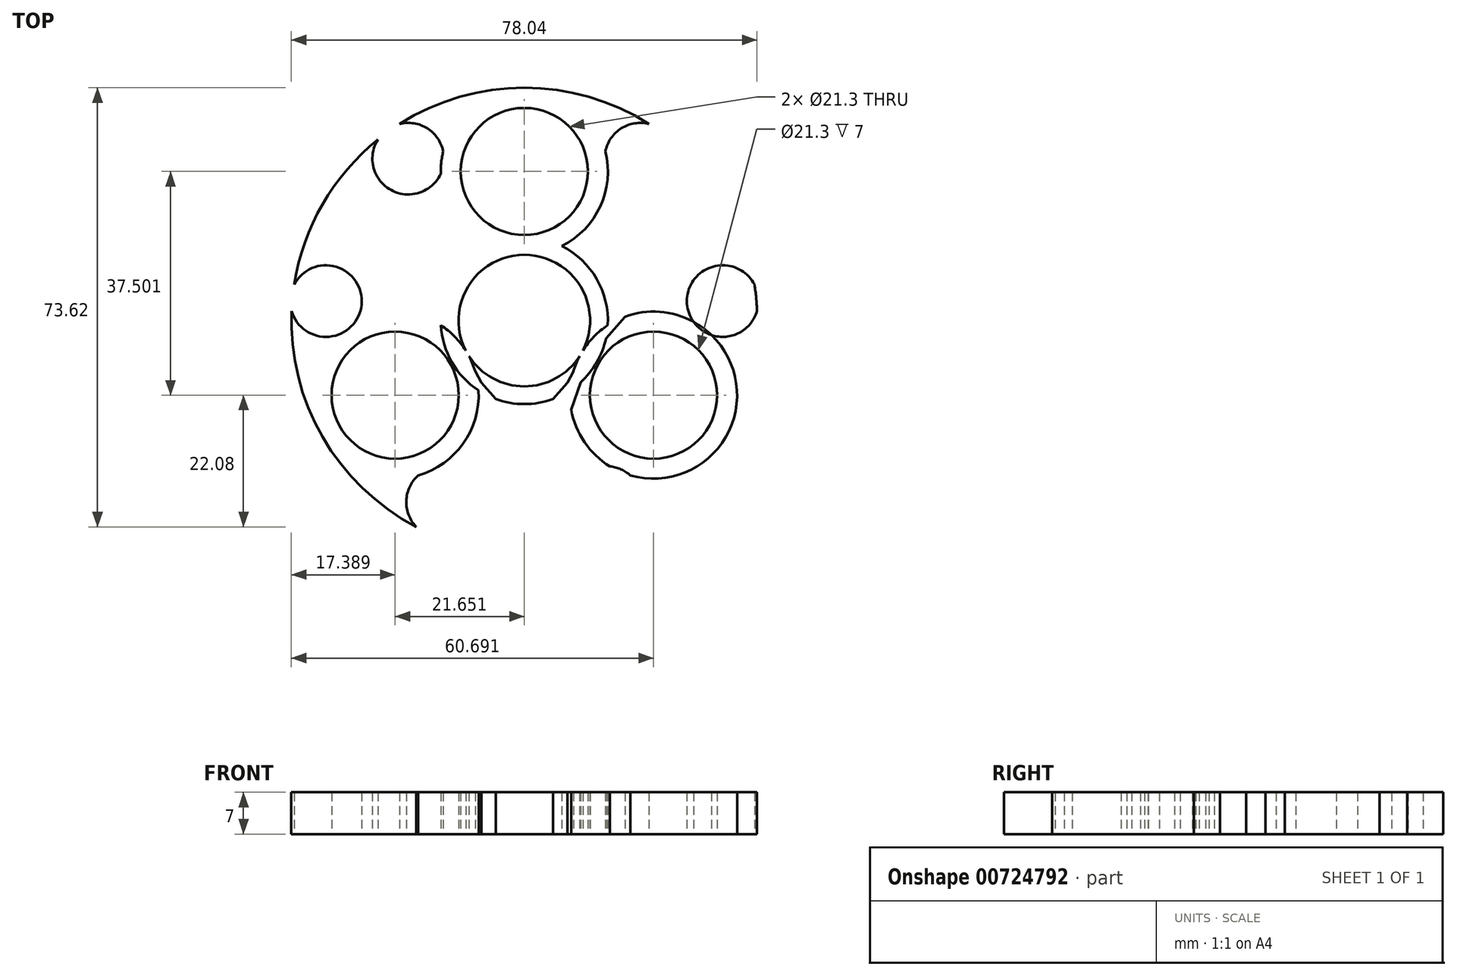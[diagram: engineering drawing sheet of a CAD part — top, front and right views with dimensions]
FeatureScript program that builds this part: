
annotation { "Feature Type Name" : "Feature", "Feature Type Description" : "" }
export const myFeature = defineFeature(function(context is Context, id is Id, definition is map)
    precondition{}
    {
        {
            var Q0;
            Q0=qCreatedBy(makeId("Top.planeOp"),FACE);
            var sketch = newSketch(context, id + "F0", { "sketchPlane" : qUnion([Q0])});
            skCircle(sketch, "E0", {"center": v(0, 0) * mm, "radius": 11.03 * mm});
            skCircle(sketch, "E1", {"center": v(0, 0) * mm, "radius": 14 * mm});
            skCircle(sketch, "E2", {"center": v(0, 25) * mm, "radius": 10.65 * mm});
            skCircle(sketch, "E3", {"center": v(0, 25) * mm, "radius": 14 * mm});
            skCircle(sketch, "E4.1.2", {"center": v(-21.65, -12.5) * mm, "radius": 14 * mm});
            skCircle(sketch, "E4.1.3", {"center": v(-21.65, -12.5) * mm, "radius": 10.65 * mm});
            skCircle(sketch, "E4.2.2", {"center": v(21.65, -12.5) * mm, "radius": 14 * mm});
            skCircle(sketch, "E4.2.3", {"center": v(21.65, -12.5) * mm, "radius": 10.65 * mm});
            skCircle(sketch, "E5", {"center": v(0, 0) * mm, "radius": 39.04 * mm});
            skCircle(sketch, "E6", {"center": v(-19.46, 27.15) * mm, "radius": 6 * mm});
            skCircle(sketch, "E7.MirrorC", {"center": v(19.46, 27.15) * mm, "radius": 6 * mm});
            skCircle(sketch, "E8.1.0", {"center": v(-13.78, -30.42) * mm, "radius": 6 * mm});
            skCircle(sketch, "E8.1.1", {"center": v(-33.24, 3.28) * mm, "radius": 6 * mm});
            skCircle(sketch, "E8.2.0", {"center": v(33.24, 3.28) * mm, "radius": 6 * mm});
            skCircle(sketch, "E8.2.1", {"center": v(13.78, -30.42) * mm, "radius": 6 * mm});
            skSolve(sketch);
        }
        {
            var Q0;
            {var subQ0=sQuery(id+"F0.wireOp",EDGE,"E6");var subQ1=sQuery(id+"F0.wireOp",EDGE,"E3");var subQ2=makeQuery(id+"F0.imprint","INTERSECT",VERTEX,{"disambiguationData":[OD(0.0)],"derivedFrom":[subQ1,subQ0]});Q0=makeQuery(id+"F0.imprint","IMPRINT",FACE,{"disambiguationData":[TD([[makeQuery(id+"F0.imprint","IMPRINT",EDGE,{"disambiguationData":[TD([[subQ2,1.0]])],"derivedFrom":subQ1}),-1.0]])]});}
            var Q1;
            {var subQ0=sQuery(id+"F0.wireOp",EDGE,"E8.1.0");var subQ1=sQuery(id+"F0.wireOp",EDGE,"E4.1.2");var subQ2=makeQuery(id+"F0.imprint","INTERSECT",VERTEX,{"disambiguationData":[OD(0.0)],"derivedFrom":[subQ1,subQ0]});Q1=makeQuery(id+"F0.imprint","IMPRINT",FACE,{"disambiguationData":[TD([[makeQuery(id+"F0.imprint","IMPRINT",EDGE,{"disambiguationData":[TD([[subQ2,1.0]])],"derivedFrom":subQ1}),-1.0]])]});}
            var Q2;
            {var subQ0=sQuery(id+"F0.wireOp",EDGE,"E8.2.0");var subQ1=sQuery(id+"F0.wireOp",EDGE,"E4.2.2");var subQ2=makeQuery(id+"F0.imprint","INTERSECT",VERTEX,{"disambiguationData":[OD(0.0)],"derivedFrom":[subQ1,subQ0]});Q2=makeQuery(id+"F0.imprint","IMPRINT",FACE,{"disambiguationData":[TD([[makeQuery(id+"F0.imprint","IMPRINT",EDGE,{"disambiguationData":[TD([[subQ2,1.0]])],"derivedFrom":subQ1}),-1.0]])]});}
            var Q3;
            Q3=makeQuery(id+"F0.imprint","IMPRINT",FACE,{"disambiguationData":[TD([[makeQuery(id+"F0.imprint","IMPRINT",EDGE,{"derivedFrom":sQuery(id+"F0.wireOp",EDGE,"E2")}),-1.0]])]});
            var Q4;
            {var subQ0=sQuery(id+"F0.wireOp",EDGE,"E0");var subQ1=sQuery(id+"F0.wireOp",EDGE,"E3");var subQ2=makeQuery(id+"F0.imprint","INTERSECT",VERTEX,{"disambiguationData":[OD(1.0)],"derivedFrom":[subQ1,subQ0]});Q4=makeQuery(id+"F0.imprint","IMPRINT",FACE,{"disambiguationData":[TD([[makeQuery(id+"F0.imprint","IMPRINT",EDGE,{"disambiguationData":[TD([[subQ2,-1.0]])],"derivedFrom":subQ1}),-1.0]])]});}
            var Q5;
            {var subQ0=sQuery(id+"F0.wireOp",EDGE,"E1");var subQ1=sQuery(id+"F0.wireOp",EDGE,"E3");var subQ2=makeQuery(id+"F0.imprint","INTERSECT",VERTEX,{"disambiguationData":[OD(0.0)],"derivedFrom":[subQ1,subQ0]});Q5=makeQuery(id+"F0.imprint","IMPRINT",FACE,{"disambiguationData":[TD([[makeQuery(id+"F0.imprint","IMPRINT",EDGE,{"disambiguationData":[TD([[subQ2,-1.0]])],"derivedFrom":subQ1}),-1.0]])]});}
            var Q6;
            {var subQ0=sQuery(id+"F0.wireOp",EDGE,"E1");var subQ1=sQuery(id+"F0.wireOp",EDGE,"E4.1.2");var subQ2=makeQuery(id+"F0.imprint","INTERSECT",VERTEX,{"disambiguationData":[OD(0.0)],"derivedFrom":[subQ1,subQ0]});Q6=makeQuery(id+"F0.imprint","IMPRINT",FACE,{"disambiguationData":[TD([[makeQuery(id+"F0.imprint","IMPRINT",EDGE,{"disambiguationData":[TD([[subQ2,-1.0]])],"derivedFrom":subQ1}),1.0]])]});}
            var Q7;
            {var subQ0=sQuery(id+"F0.wireOp",EDGE,"E1");var subQ1=sQuery(id+"F0.wireOp",EDGE,"E4.1.2");var subQ2=makeQuery(id+"F0.imprint","INTERSECT",VERTEX,{"disambiguationData":[OD(0.0)],"derivedFrom":[subQ1,subQ0]});Q7=makeQuery(id+"F0.imprint","IMPRINT",FACE,{"disambiguationData":[TD([[makeQuery(id+"F0.imprint","IMPRINT",EDGE,{"disambiguationData":[TD([[subQ2,-1.0]])],"derivedFrom":subQ1}),-1.0]])]});}
            var Q8;
            {var subQ0=sQuery(id+"F0.wireOp",EDGE,"E1");var subQ1=sQuery(id+"F0.wireOp",EDGE,"E3");var subQ2=makeQuery(id+"F0.imprint","INTERSECT",VERTEX,{"disambiguationData":[OD(0.0)],"derivedFrom":[subQ1,subQ0]});Q8=makeQuery(id+"F0.imprint","IMPRINT",FACE,{"disambiguationData":[TD([[makeQuery(id+"F0.imprint","IMPRINT",EDGE,{"disambiguationData":[TD([[subQ2,-1.0]])],"derivedFrom":subQ1}),1.0]])]});}
            var Q9;
            {var subQ0=sQuery(id+"F0.wireOp",EDGE,"E4.2.2");var subQ1=sQuery(id+"F0.wireOp",EDGE,"E1");var subQ2=makeQuery(id+"F0.imprint","INTERSECT",VERTEX,{"disambiguationData":[OD(0.0)],"derivedFrom":[subQ1,subQ0]});Q9=makeQuery(id+"F0.imprint","IMPRINT",FACE,{"disambiguationData":[TD([[makeQuery(id+"F0.imprint","IMPRINT",EDGE,{"disambiguationData":[TD([[subQ2,1.0]])],"derivedFrom":subQ1}),1.0]])]});}
            var Q10;
            Q10=makeQuery(id+"F0.imprint","IMPRINT",FACE,{"disambiguationData":[TD([[makeQuery(id+"F0.imprint","IMPRINT",EDGE,{"derivedFrom":sQuery(id+"F0.wireOp",EDGE,"E4.2.3")}),-1.0]])]});
            var Q11;
            Q11=makeQuery(id+"F0.imprint","IMPRINT",FACE,{"disambiguationData":[TD([[makeQuery(id+"F0.imprint","IMPRINT",EDGE,{"derivedFrom":sQuery(id+"F0.wireOp",EDGE,"E4.1.3")}),-1.0]])]});
            var Q12;
            {var subQ0=sQuery(id+"F0.wireOp",EDGE,"E8.1.1");var subQ1=sQuery(id+"F0.wireOp",EDGE,"E4.1.2");var subQ2=makeQuery(id+"F0.imprint","INTERSECT",VERTEX,{"disambiguationData":[OD(0.0)],"derivedFrom":[subQ1,subQ0]});Q12=makeQuery(id+"F0.imprint","IMPRINT",FACE,{"disambiguationData":[TD([[makeQuery(id+"F0.imprint","IMPRINT",EDGE,{"disambiguationData":[TD([[subQ2,1.0]])],"derivedFrom":subQ1}),1.0]])]});}
            var Q13;
            {var subQ0=sQuery(id+"F0.wireOp",EDGE,"E6");var subQ1=sQuery(id+"F0.wireOp",EDGE,"E3");var subQ2=makeQuery(id+"F0.imprint","INTERSECT",VERTEX,{"disambiguationData":[OD(0.0)],"derivedFrom":[subQ1,subQ0]});Q13=makeQuery(id+"F0.imprint","IMPRINT",FACE,{"disambiguationData":[TD([[makeQuery(id+"F0.imprint","IMPRINT",EDGE,{"disambiguationData":[TD([[subQ2,-1.0]])],"derivedFrom":subQ1}),1.0]])]});}
            var Q14;
            {var subQ0=sQuery(id+"F0.wireOp",EDGE,"E7.MirrorC");var subQ1=sQuery(id+"F0.wireOp",EDGE,"E3");var subQ2=makeQuery(id+"F0.imprint","INTERSECT",VERTEX,{"disambiguationData":[OD(0.0)],"derivedFrom":[subQ1,subQ0]});Q14=makeQuery(id+"F0.imprint","IMPRINT",FACE,{"disambiguationData":[TD([[makeQuery(id+"F0.imprint","IMPRINT",EDGE,{"disambiguationData":[TD([[subQ2,1.0]])],"derivedFrom":subQ1}),1.0]])]});}
            var Q15;
            {var subQ0=sQuery(id+"F0.wireOp",EDGE,"E8.2.0");var subQ1=sQuery(id+"F0.wireOp",EDGE,"E4.2.2");var subQ2=makeQuery(id+"F0.imprint","INTERSECT",VERTEX,{"disambiguationData":[OD(0.0)],"derivedFrom":[subQ1,subQ0]});Q15=makeQuery(id+"F0.imprint","IMPRINT",FACE,{"disambiguationData":[TD([[makeQuery(id+"F0.imprint","IMPRINT",EDGE,{"disambiguationData":[TD([[subQ2,-1.0]])],"derivedFrom":subQ1}),1.0]])]});}
            var Q16;
            {var subQ0=sQuery(id+"F0.wireOp",EDGE,"E8.2.1");var subQ1=sQuery(id+"F0.wireOp",EDGE,"E4.2.2");var subQ2=makeQuery(id+"F0.imprint","INTERSECT",VERTEX,{"disambiguationData":[OD(0.0)],"derivedFrom":[subQ1,subQ0]});Q16=makeQuery(id+"F0.imprint","IMPRINT",FACE,{"disambiguationData":[TD([[makeQuery(id+"F0.imprint","IMPRINT",EDGE,{"disambiguationData":[TD([[subQ2,1.0]])],"derivedFrom":subQ1}),1.0]])]});}
            var Q17;
            {var subQ0=sQuery(id+"F0.wireOp",EDGE,"E8.1.0");var subQ1=sQuery(id+"F0.wireOp",EDGE,"E4.1.2");var subQ2=makeQuery(id+"F0.imprint","INTERSECT",VERTEX,{"disambiguationData":[OD(0.0)],"derivedFrom":[subQ1,subQ0]});Q17=makeQuery(id+"F0.imprint","IMPRINT",FACE,{"disambiguationData":[TD([[makeQuery(id+"F0.imprint","IMPRINT",EDGE,{"disambiguationData":[TD([[subQ2,-1.0]])],"derivedFrom":subQ1}),1.0]])]});}
            extrude(context, id + "F1", {"entities" : qUnion([Q0, Q1, Q2, Q3, Q4, Q5, Q6, Q7, Q8, Q9, Q10, Q11, Q12, Q13, Q14, Q15, Q16, Q17]), "depth" : 7 * mm, "offsetDistance" : 25 * mm});
        }
        {
            var Q0;
            {var subQ0=sQuery(id+"F0.wireOp",EDGE,"E1");var subQ1=sQuery(id+"F0.wireOp",EDGE,"E3");Q0=makeQuery(id+"F1.opExtrude","SWEPT_EDGE",EDGE,{"disambiguationData":[OSD([subQ1,subQ0]),TDD([makeQuery(id+"F0.imprint","INTERSECT",VERTEX,{"disambiguationData":[OD(1.0)],"derivedFrom":[subQ1,subQ0]})])]});}
            var Q1;
            {var subQ0=sQuery(id+"F0.wireOp",EDGE,"E4.2.2");var subQ1=sQuery(id+"F0.wireOp",EDGE,"E1");Q1=makeQuery(id+"F1.opExtrude","SWEPT_EDGE",EDGE,{"disambiguationData":[OSD([subQ1,subQ0]),TDD([makeQuery(id+"F0.imprint","INTERSECT",VERTEX,{"disambiguationData":[OD(0.0)],"derivedFrom":[subQ1,subQ0]})])]});}
            var Q2;
            {var subQ0=sQuery(id+"F0.wireOp",EDGE,"E1");var subQ1=sQuery(id+"F0.wireOp",EDGE,"E3");Q2=makeQuery(id+"F1.opExtrude","SWEPT_EDGE",EDGE,{"disambiguationData":[OSD([subQ1,subQ0]),TDD([makeQuery(id+"F0.imprint","INTERSECT",VERTEX,{"disambiguationData":[OD(0.0)],"derivedFrom":[subQ1,subQ0]})])]});}
            var Q3;
            {var subQ0=sQuery(id+"F0.wireOp",EDGE,"E1");var subQ1=sQuery(id+"F0.wireOp",EDGE,"E4.1.2");Q3=makeQuery(id+"F1.opExtrude","SWEPT_EDGE",EDGE,{"disambiguationData":[OSD([subQ1,subQ0]),TDD([makeQuery(id+"F0.imprint","INTERSECT",VERTEX,{"disambiguationData":[OD(1.0)],"derivedFrom":[subQ1,subQ0]})])]});}
            var Q4;
            {var subQ0=sQuery(id+"F0.wireOp",EDGE,"E1");var subQ1=sQuery(id+"F0.wireOp",EDGE,"E4.1.2");Q4=makeQuery(id+"F1.opExtrude","SWEPT_EDGE",EDGE,{"disambiguationData":[OSD([subQ1,subQ0]),TDD([makeQuery(id+"F0.imprint","INTERSECT",VERTEX,{"disambiguationData":[OD(0.0)],"derivedFrom":[subQ1,subQ0]})])]});}
            var Q5;
            {var subQ0=sQuery(id+"F0.wireOp",EDGE,"E4.2.2");var subQ1=sQuery(id+"F0.wireOp",EDGE,"E1");Q5=makeQuery(id+"F1.opExtrude","SWEPT_EDGE",EDGE,{"disambiguationData":[OSD([subQ1,subQ0]),TDD([makeQuery(id+"F0.imprint","INTERSECT",VERTEX,{"disambiguationData":[OD(1.0)],"derivedFrom":[subQ1,subQ0]})])]});}
            chamfer(context, id + "F2", {"entities" : qUnion([Q0, Q1, Q2, Q3, Q4, Q5]), "width" : 5 * mm, "tangentPropagation" : true});
        }
        {
            var Q0;
            {var subQ0=sQuery(id+"F0.wireOp",EDGE,"E8.2.1");var subQ1=sQuery(id+"F0.wireOp",EDGE,"E4.2.2");var subQ3=sQuery(id+"F0.wireOp",EDGE,"E1");var subQ4=makeQuery(id+"F0.imprint","INTERSECT",VERTEX,{"disambiguationData":[OD(1.0)],"derivedFrom":[subQ3,subQ1]});Q0=makeQuery(id+"F2.opChamfer","BLEND_EDGE",EDGE,{"blendedFrom":[makeQuery(id+"F1.opExtrude","SWEPT_EDGE",EDGE,{"disambiguationData":[OSD([subQ3,subQ1]),TDD([subQ4])]}),makeQuery(id+"F1.opExtrude","SWEPT_FACE",FACE,{"disambiguationData":[OSD([subQ1]),TDD([makeQuery(id+"F0.imprint","IMPRINT",EDGE,{"disambiguationData":[TD([[subQ4,-1.0]])],"derivedFrom":subQ1}),makeQuery(id+"F0.imprint","IMPRINT",EDGE,{"disambiguationData":[TD([[makeQuery(id+"F0.imprint","INTERSECT",VERTEX,{"disambiguationData":[OD(0.0)],"derivedFrom":[subQ1,subQ0]}),1.0]])],"derivedFrom":subQ1})])]})],"blendedInto":[makeQuery(id+"F1.opExtrude","SWEPT_FACE",FACE,{"disambiguationData":[OSD([subQ1]),TDD([makeQuery(id+"F0.imprint","IMPRINT",EDGE,{"disambiguationData":[TD([[subQ4,-1.0]])],"derivedFrom":subQ1}),makeQuery(id+"F0.imprint","IMPRINT",EDGE,{"disambiguationData":[TD([[makeQuery(id+"F0.imprint","INTERSECT",VERTEX,{"disambiguationData":[OD(0.0)],"derivedFrom":[subQ1,subQ0]}),1.0]])],"derivedFrom":subQ1})])]})]});}
            var Q1;
            {var subQ0=sQuery(id+"F0.wireOp",EDGE,"E8.1.0");var subQ1=sQuery(id+"F0.wireOp",EDGE,"E4.1.2");var subQ2=makeQuery(id+"F0.imprint","INTERSECT",VERTEX,{"disambiguationData":[OD(1.0)],"derivedFrom":[subQ1,subQ0]});var subQ3=sQuery(id+"F0.wireOp",EDGE,"E1");var subQ4=makeQuery(id+"F0.imprint","INTERSECT",VERTEX,{"disambiguationData":[OD(0.0)],"derivedFrom":[subQ1,subQ3]});Q1=makeQuery(id+"F2.opChamfer","BLEND_EDGE",EDGE,{"blendedFrom":[makeQuery(id+"F1.opExtrude","SWEPT_EDGE",EDGE,{"disambiguationData":[OSD([subQ1,subQ3]),TDD([subQ4])]}),makeQuery(id+"F1.opExtrude","SWEPT_FACE",FACE,{"disambiguationData":[OSD([subQ1]),TDD([makeQuery(id+"F0.imprint","IMPRINT",EDGE,{"disambiguationData":[TD([[makeQuery(id+"F0.imprint","INTERSECT",VERTEX,{"disambiguationData":[OD(0.0)],"derivedFrom":[subQ1,subQ0]}),-1.0]])],"derivedFrom":subQ1}),makeQuery(id+"F0.imprint","IMPRINT",EDGE,{"disambiguationData":[TD([[subQ2,-1.0]])],"derivedFrom":subQ1})])]})],"blendedInto":[makeQuery(id+"F1.opExtrude","SWEPT_FACE",FACE,{"disambiguationData":[OSD([subQ1]),TDD([makeQuery(id+"F0.imprint","IMPRINT",EDGE,{"disambiguationData":[TD([[makeQuery(id+"F0.imprint","INTERSECT",VERTEX,{"disambiguationData":[OD(0.0)],"derivedFrom":[subQ1,subQ0]}),-1.0]])],"derivedFrom":subQ1}),makeQuery(id+"F0.imprint","IMPRINT",EDGE,{"disambiguationData":[TD([[subQ2,-1.0]])],"derivedFrom":subQ1})])]})]});}
            var Q2;
            {var subQ0=sQuery(id+"F0.wireOp",EDGE,"E4.2.2");var subQ1=sQuery(id+"F0.wireOp",EDGE,"E1");var subQ2=makeQuery(id+"F0.imprint","INTERSECT",VERTEX,{"disambiguationData":[OD(0.0)],"derivedFrom":[subQ1,subQ0]});var subQ3=sQuery(id+"F0.wireOp",EDGE,"E8.2.0");Q2=makeQuery(id+"F2.opChamfer","BLEND_EDGE",EDGE,{"blendedFrom":[makeQuery(id+"F1.opExtrude","SWEPT_EDGE",EDGE,{"disambiguationData":[OSD([subQ1,subQ0]),TDD([subQ2])]}),makeQuery(id+"F1.opExtrude","SWEPT_FACE",FACE,{"disambiguationData":[OSD([subQ0]),TDD([makeQuery(id+"F0.imprint","IMPRINT",EDGE,{"disambiguationData":[TD([[makeQuery(id+"F0.imprint","INTERSECT",VERTEX,{"disambiguationData":[OD(0.0)],"derivedFrom":[subQ0,subQ3]}),-1.0]])],"derivedFrom":subQ0}),makeQuery(id+"F0.imprint","IMPRINT",EDGE,{"disambiguationData":[TD([[subQ2,1.0]])],"derivedFrom":subQ0})])]})],"blendedInto":[makeQuery(id+"F1.opExtrude","SWEPT_FACE",FACE,{"disambiguationData":[OSD([subQ0]),TDD([makeQuery(id+"F0.imprint","IMPRINT",EDGE,{"disambiguationData":[TD([[makeQuery(id+"F0.imprint","INTERSECT",VERTEX,{"disambiguationData":[OD(0.0)],"derivedFrom":[subQ0,subQ3]}),-1.0]])],"derivedFrom":subQ0}),makeQuery(id+"F0.imprint","IMPRINT",EDGE,{"disambiguationData":[TD([[subQ2,1.0]])],"derivedFrom":subQ0})])]})]});}
            var Q3;
            {var subQ0=sQuery(id+"F0.wireOp",EDGE,"E8.1.1");var subQ1=sQuery(id+"F0.wireOp",EDGE,"E4.1.2");var subQ3=sQuery(id+"F0.wireOp",EDGE,"E1");var subQ4=makeQuery(id+"F0.imprint","INTERSECT",VERTEX,{"disambiguationData":[OD(1.0)],"derivedFrom":[subQ1,subQ3]});Q3=makeQuery(id+"F2.opChamfer","BLEND_EDGE",EDGE,{"blendedFrom":[makeQuery(id+"F1.opExtrude","SWEPT_EDGE",EDGE,{"disambiguationData":[OSD([subQ1,subQ3]),TDD([subQ4])]}),makeQuery(id+"F1.opExtrude","SWEPT_FACE",FACE,{"disambiguationData":[OSD([subQ1]),TDD([makeQuery(id+"F0.imprint","IMPRINT",EDGE,{"disambiguationData":[TD([[subQ4,-1.0]])],"derivedFrom":subQ1}),makeQuery(id+"F0.imprint","IMPRINT",EDGE,{"disambiguationData":[TD([[makeQuery(id+"F0.imprint","INTERSECT",VERTEX,{"disambiguationData":[OD(0.0)],"derivedFrom":[subQ1,subQ0]}),1.0]])],"derivedFrom":subQ1})])]})],"blendedInto":[makeQuery(id+"F1.opExtrude","SWEPT_FACE",FACE,{"disambiguationData":[OSD([subQ1]),TDD([makeQuery(id+"F0.imprint","IMPRINT",EDGE,{"disambiguationData":[TD([[subQ4,-1.0]])],"derivedFrom":subQ1}),makeQuery(id+"F0.imprint","IMPRINT",EDGE,{"disambiguationData":[TD([[makeQuery(id+"F0.imprint","INTERSECT",VERTEX,{"disambiguationData":[OD(0.0)],"derivedFrom":[subQ1,subQ0]}),1.0]])],"derivedFrom":subQ1})])]})]});}
            var Q4;
            {var subQ0=sQuery(id+"F0.wireOp",EDGE,"E6");var subQ1=sQuery(id+"F0.wireOp",EDGE,"E3");var subQ2=makeQuery(id+"F0.imprint","INTERSECT",VERTEX,{"disambiguationData":[OD(1.0)],"derivedFrom":[subQ1,subQ0]});var subQ3=sQuery(id+"F0.wireOp",EDGE,"E1");var subQ4=makeQuery(id+"F0.imprint","INTERSECT",VERTEX,{"disambiguationData":[OD(0.0)],"derivedFrom":[subQ1,subQ3]});Q4=makeQuery(id+"F2.opChamfer","BLEND_EDGE",EDGE,{"blendedFrom":[makeQuery(id+"F1.opExtrude","SWEPT_EDGE",EDGE,{"disambiguationData":[OSD([subQ1,subQ3]),TDD([subQ4])]}),makeQuery(id+"F1.opExtrude","SWEPT_FACE",FACE,{"disambiguationData":[OSD([subQ1]),TDD([makeQuery(id+"F0.imprint","IMPRINT",EDGE,{"disambiguationData":[TD([[makeQuery(id+"F0.imprint","INTERSECT",VERTEX,{"disambiguationData":[OD(0.0)],"derivedFrom":[subQ1,subQ0]}),-1.0]])],"derivedFrom":subQ1}),makeQuery(id+"F0.imprint","IMPRINT",EDGE,{"disambiguationData":[TD([[subQ2,-1.0]])],"derivedFrom":subQ1})])]})],"blendedInto":[makeQuery(id+"F1.opExtrude","SWEPT_FACE",FACE,{"disambiguationData":[OSD([subQ1]),TDD([makeQuery(id+"F0.imprint","IMPRINT",EDGE,{"disambiguationData":[TD([[makeQuery(id+"F0.imprint","INTERSECT",VERTEX,{"disambiguationData":[OD(0.0)],"derivedFrom":[subQ1,subQ0]}),-1.0]])],"derivedFrom":subQ1}),makeQuery(id+"F0.imprint","IMPRINT",EDGE,{"disambiguationData":[TD([[subQ2,-1.0]])],"derivedFrom":subQ1})])]})]});}
            var Q5;
            {var subQ0=sQuery(id+"F0.wireOp",EDGE,"E7.MirrorC");var subQ1=sQuery(id+"F0.wireOp",EDGE,"E3");var subQ3=sQuery(id+"F0.wireOp",EDGE,"E1");var subQ4=makeQuery(id+"F0.imprint","INTERSECT",VERTEX,{"disambiguationData":[OD(1.0)],"derivedFrom":[subQ1,subQ3]});Q5=makeQuery(id+"F2.opChamfer","BLEND_EDGE",EDGE,{"blendedFrom":[makeQuery(id+"F1.opExtrude","SWEPT_EDGE",EDGE,{"disambiguationData":[OSD([subQ1,subQ3]),TDD([subQ4])]}),makeQuery(id+"F1.opExtrude","SWEPT_FACE",FACE,{"disambiguationData":[OSD([subQ1]),TDD([makeQuery(id+"F0.imprint","IMPRINT",EDGE,{"disambiguationData":[TD([[subQ4,-1.0]])],"derivedFrom":subQ1}),makeQuery(id+"F0.imprint","IMPRINT",EDGE,{"disambiguationData":[TD([[makeQuery(id+"F0.imprint","INTERSECT",VERTEX,{"disambiguationData":[OD(0.0)],"derivedFrom":[subQ1,subQ0]}),1.0]])],"derivedFrom":subQ1})])]})],"blendedInto":[makeQuery(id+"F1.opExtrude","SWEPT_FACE",FACE,{"disambiguationData":[OSD([subQ1]),TDD([makeQuery(id+"F0.imprint","IMPRINT",EDGE,{"disambiguationData":[TD([[subQ4,-1.0]])],"derivedFrom":subQ1}),makeQuery(id+"F0.imprint","IMPRINT",EDGE,{"disambiguationData":[TD([[makeQuery(id+"F0.imprint","INTERSECT",VERTEX,{"disambiguationData":[OD(0.0)],"derivedFrom":[subQ1,subQ0]}),1.0]])],"derivedFrom":subQ1})])]})]});}
            chamfer(context, id + "F3", {"entities" : qUnion([Q0, Q1, Q2, Q3, Q4, Q5]), "width" : 5 * mm, "tangentPropagation" : true});
        }
    });
